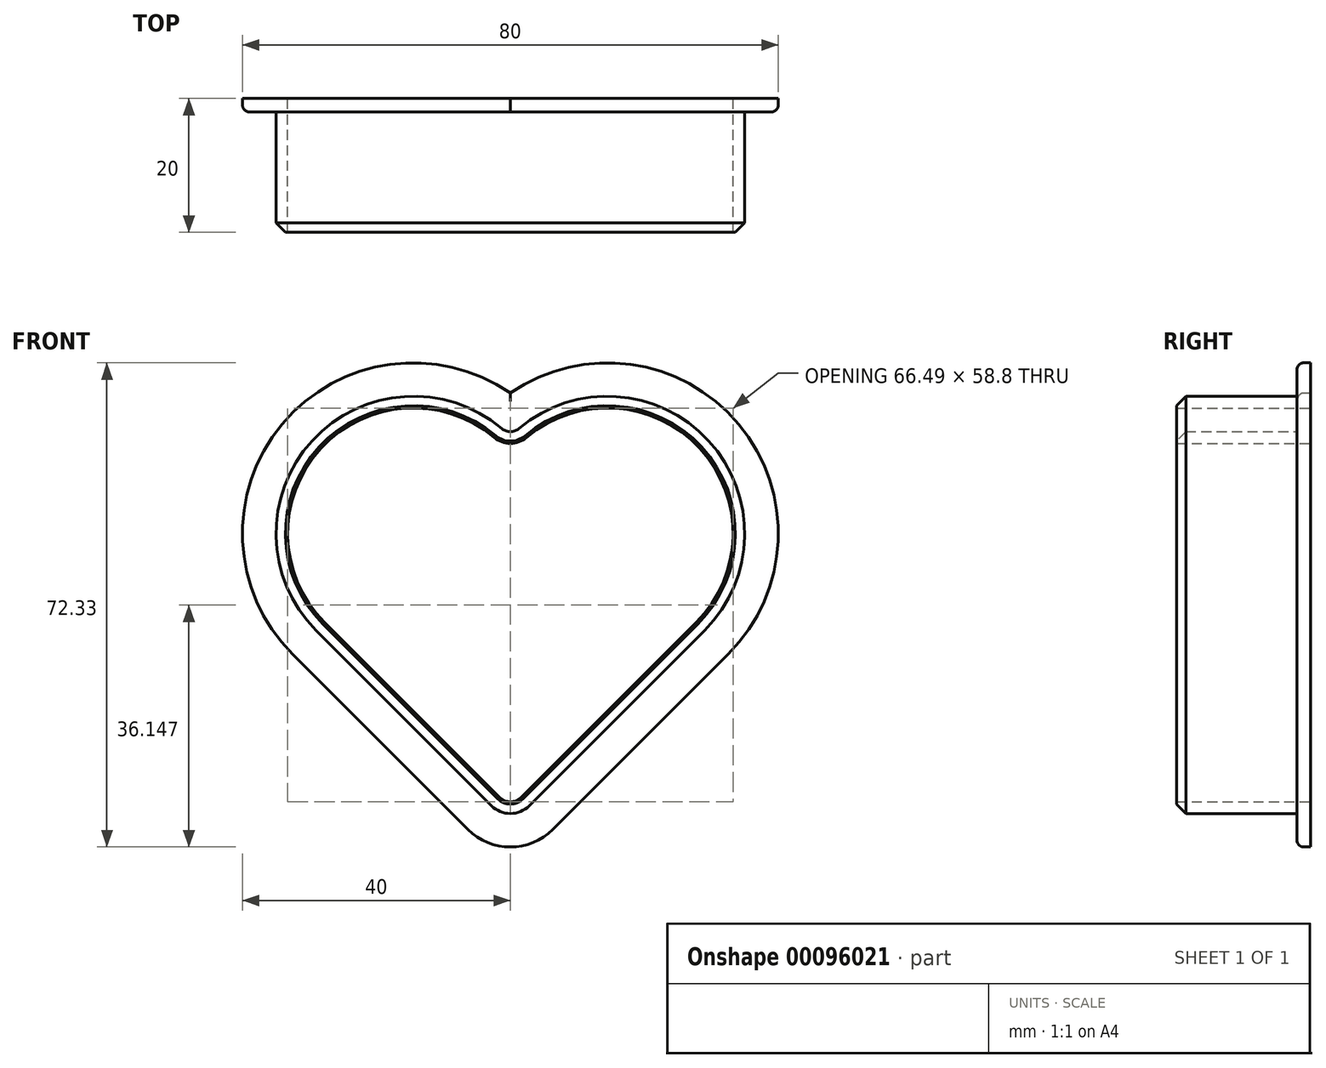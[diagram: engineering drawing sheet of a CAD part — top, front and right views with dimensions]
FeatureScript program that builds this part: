
annotation { "Feature Type Name" : "Feature", "Feature Type Description" : "" }
export const myFeature = defineFeature(function(context is Context, id is Id, definition is map)
    precondition{}
    {
        {
            var Q0;
            Q0=qCreatedBy(makeId("Front.planeOp"),FACE);
            var sketch = newSketch(context, id + "F0", { "sketchPlane" : qUnion([Q0])});
            skLineSegment(sketch, "E0", {"start": v(-2.83, 2.83) * mm, "end": v(-29, 29) * mm});
            skLineSegment(sketch, "E1", {"start": v(2.83, 2.83) * mm, "end": v(29, 29) * mm});
            skArc(sketch, "E2", {"start": v(29, 29) * mm, "mid": v(29.6, 57.36) * mm, "end": v(1.29, 59.17) * mm});
            skArc(sketch, "E3", {"start": v(-1.29, 59.17) * mm, "mid": v(-29.6, 57.36) * mm, "end": v(-29, 29) * mm});
            skPoint(sketch, "E4.orphan", {"position": v(0, 29) * mm});
            skPoint(sketch, "E5.visualSharp", {"position": v(0, 57.99) * mm});
            skArc(sketch, "E5.filletArc", {"start": v(-1.29, 59.17) * mm, "mid": v(0, 58.7) * mm, "end": v(1.29, 59.17) * mm});
            skLineSegment(sketch, "E6", {"start": v(35, 43.5) * mm, "end": v(35, 83.5) * mm, "construction": true});
            skLineSegment(sketch, "E7", {"start": v(-35, 43.5) * mm, "end": v(-35, 83.5) * mm, "construction": true});
            skLineSegment(sketch, "E8", {"start": v(-35, 83.5) * mm, "end": v(35, 83.5) * mm, "construction": true});
            skPoint(sketch, "E9.visualSharp", {"position": v(0, 0) * mm});
            skArc(sketch, "E9.filletArc", {"start": v(-2.83, 2.83) * mm, "mid": v(0, 1.66) * mm, "end": v(2.83, 2.83) * mm});
            skLineSegment(sketch, "E10.0", {"start": v(6.36, -0.7) * mm, "end": v(32.53, 25.46) * mm});
            skArc(sketch, "E10.1", {"start": v(-6.36, -0.7) * mm, "mid": v(0, -3.34) * mm, "end": v(6.36, -0.7) * mm});
            skArc(sketch, "E10.2", {"start": v(32.53, 25.46) * mm, "mid": v(34.08, 59.82) * mm, "end": v(0, 64.47) * mm});
            skArc(sketch, "E10.3", {"start": v(0, 64.47) * mm, "mid": v(-34.08, 59.82) * mm, "end": v(-32.53, 25.46) * mm});
            skLineSegment(sketch, "E10.4", {"start": v(-6.36, -0.7) * mm, "end": v(-32.53, 25.46) * mm});
            skLineSegment(sketch, "E11.0", {"start": v(-1.6, 4.07) * mm, "end": v(-27.76, 30.23) * mm});
            skArc(sketch, "E11.1", {"start": v(-2.42, 57.83) * mm, "mid": v(-28.31, 56.17) * mm, "end": v(-27.76, 30.23) * mm});
            skLineSegment(sketch, "E11.2", {"start": v(1.6, 4.07) * mm, "end": v(27.76, 30.23) * mm});
            skArc(sketch, "E11.3", {"start": v(27.76, 30.23) * mm, "mid": v(28.31, 56.17) * mm, "end": v(2.42, 57.83) * mm});
            skArc(sketch, "E11.4", {"start": v(-2.42, 57.83) * mm, "mid": v(0, 56.95) * mm, "end": v(2.42, 57.83) * mm});
            skPoint(sketch, "E12.visualSharp", {"position": v(0, 2.47) * mm});
            skArc(sketch, "E12.filletArc", {"start": v(-1.6, 4.07) * mm, "mid": v(0, 3.4) * mm, "end": v(1.6, 4.07) * mm});
            skSolve(sketch);
        }
        {
            var Q0;
            Q0=makeQuery(id+"F0.imprint","IMPRINT",FACE,{"disambiguationData":[TD([[makeQuery(id+"F0.imprint","IMPRINT",EDGE,{"derivedFrom":sQuery(id+"F0.wireOp",EDGE,"E0")}),-1.0]])]});
            extrude(context, id + "F1", {"entities" : qUnion([Q0]), "depth" : 20 * mm});
        }
        {
            var Q0;
            Q0=makeQuery(id+"F0.imprint","IMPRINT",FACE,{"disambiguationData":[TD([[makeQuery(id+"F0.imprint","IMPRINT",EDGE,{"derivedFrom":sQuery(id+"F0.wireOp",EDGE,"E0")}),1.0]])]});
            extrude(context, id + "F2", {"entities" : qUnion([Q0]), "operationType" : NewBodyOperationType.ADD, "depth" : 2 * mm});
        }
        {
            var Q0;
            Q0=makeQuery(id+"F1.opExtrude","CAP_EDGE",EDGE,{"disambiguationData":[OSD([sQuery(id+"F0.wireOp",EDGE,"E1")])],"isStart":false});
            chamfer(context, id + "F3", {"entities" : qUnion([Q0]), "width" : 1.4 * mm, "tangentPropagation" : true});
        }
        {
            var Q0;
            Q0=makeQuery(id+"F2.opExtrude","CAP_EDGE",EDGE,{"disambiguationData":[OSD([sQuery(id+"F0.wireOp",EDGE,"E1")])],"isStart":false});
            var Q1;
            Q1=makeQuery(id+"F2.opExtrude","CAP_EDGE",EDGE,{"disambiguationData":[OSD([sQuery(id+"F0.wireOp",EDGE,"E10.0")])],"isStart":false});
            fillet(context, id + "F4", {"entities" : qUnion([Q0, Q1]), "radius" : 1 * mm, "tangentPropagation" : true, "allowEdgeOverflow" : false});
        }
    });
